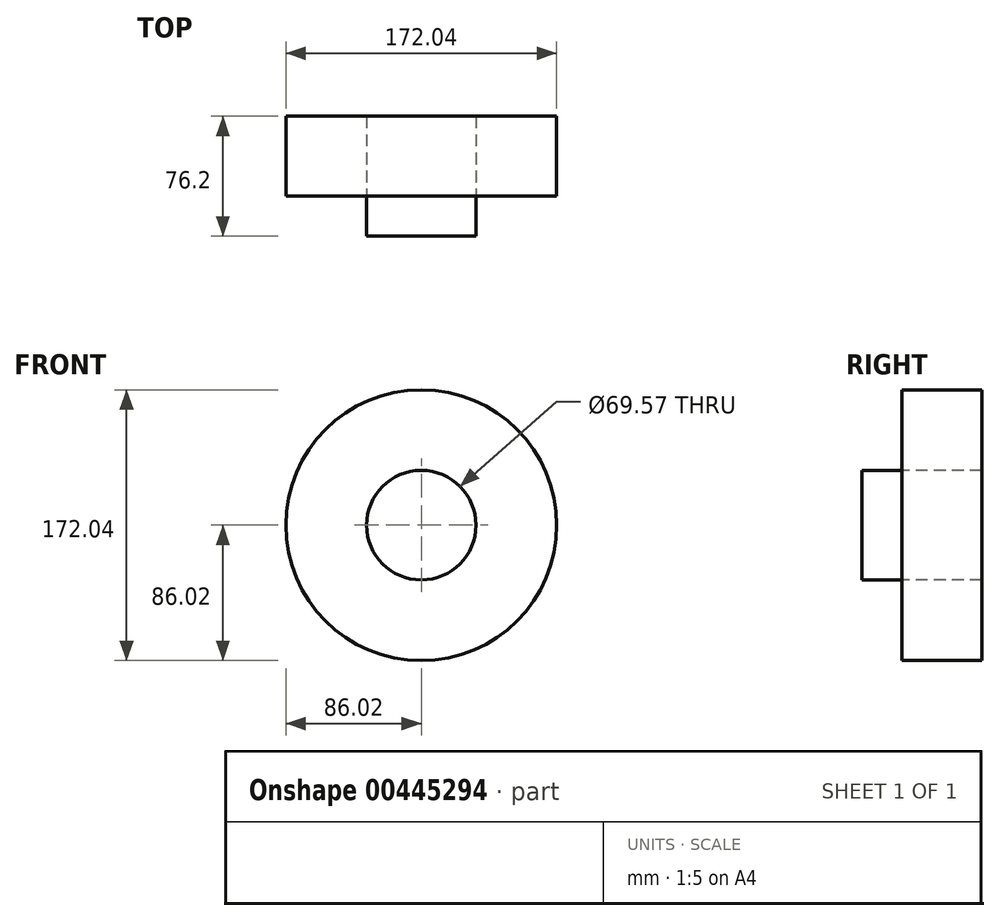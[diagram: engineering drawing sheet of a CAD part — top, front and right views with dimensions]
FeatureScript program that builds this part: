
annotation { "Feature Type Name" : "Feature", "Feature Type Description" : "" }
export const myFeature = defineFeature(function(context is Context, id is Id, definition is map)
    precondition{}
    {
        {
            var Q0;
            Q0=qCreatedBy(makeId("Front.planeOp"),FACE);
            var sketch = newSketch(context, id + "F0", { "sketchPlane" : qUnion([Q0])});
            skCircle(sketch, "E0", {"center": v(0, 0) * mm, "radius": 34.78 * mm});
            skCircle(sketch, "E1", {"center": v(0, 0) * mm, "radius": 86.02 * mm});
            skSolve(sketch);
        }
        {
            var Q0;
            Q0=makeQuery(id+"F0.imprint","IMPRINT",FACE,{"disambiguationData":[TD([[makeQuery(id+"F0.imprint","IMPRINT",EDGE,{"derivedFrom":sQuery(id+"F0.wireOp",EDGE,"E0")}),1.0]])]});
            extrude(context, id + "F1", {"entities" : qUnion([Q0]), "depth" : 25.4 * mm, "offsetDistance" : 25.4 * mm});
        }
        {
            var Q0;
            Q0 = qSketchRegion(id + "F0", true);
            extrude(context, id + "F2", {"entities" : qUnion([Q0]), "operationType" : NewBodyOperationType.ADD, "oppositeDirection" : true, "depth" : 50.8 * mm, "offsetDistance" : 25.4 * mm});
        }
    });
